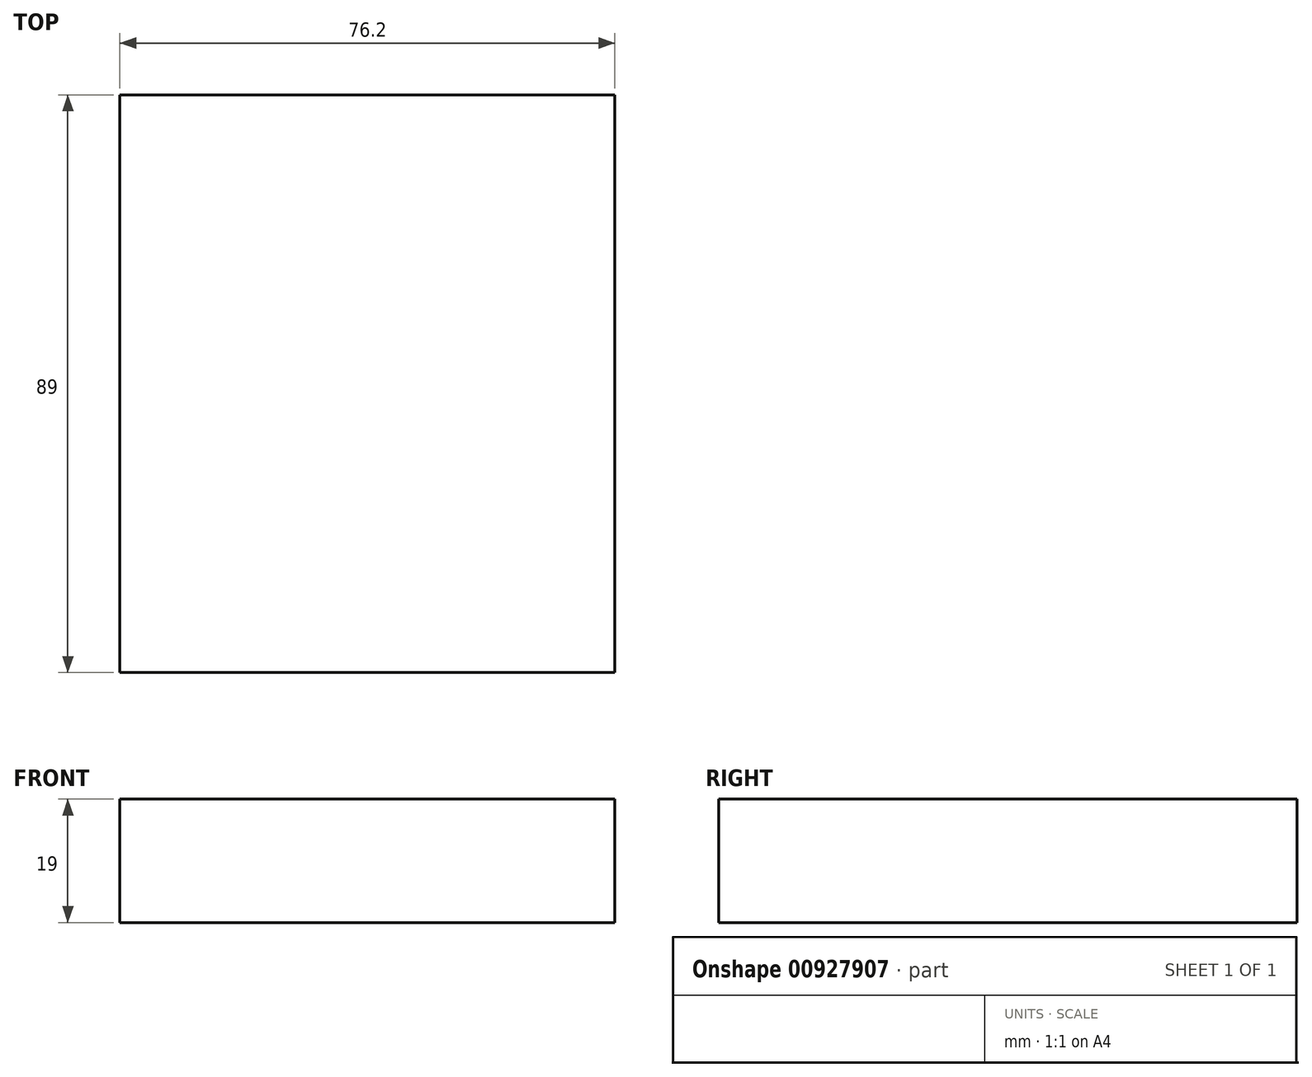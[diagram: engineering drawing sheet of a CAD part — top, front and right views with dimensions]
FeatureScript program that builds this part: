
annotation { "Feature Type Name" : "Feature", "Feature Type Description" : "" }
export const myFeature = defineFeature(function(context is Context, id is Id, definition is map)
    precondition{}
    {
        {
            var Q0;
            Q0=qCreatedBy(makeId("Right.planeOp"),FACE);
            var sketch = newSketch(context, id + "F0", { "sketchPlane" : qUnion([Q0])});
            skLineSegment(sketch, "E0.bottom", {"start": v(0, 0) * mm, "end": v(89, 0) * mm});
            skLineSegment(sketch, "E0.top", {"start": v(0, 19) * mm, "end": v(89, 19) * mm});
            skLineSegment(sketch, "E0.left", {"start": v(0, 0) * mm, "end": v(0, 19) * mm});
            skLineSegment(sketch, "E0.right", {"start": v(89, 0) * mm, "end": v(89, 19) * mm});
            skSolve(sketch);
        }
        {
            var Q0;
            Q0 = qSketchRegion(id + "F0", true);
            extrude(context, id + "F1", {"entities" : qUnion([Q0]), "depth" : (80 - (2 * 1.9)) * mm, "offsetDistance" : 25 * mm});
        }
    });
